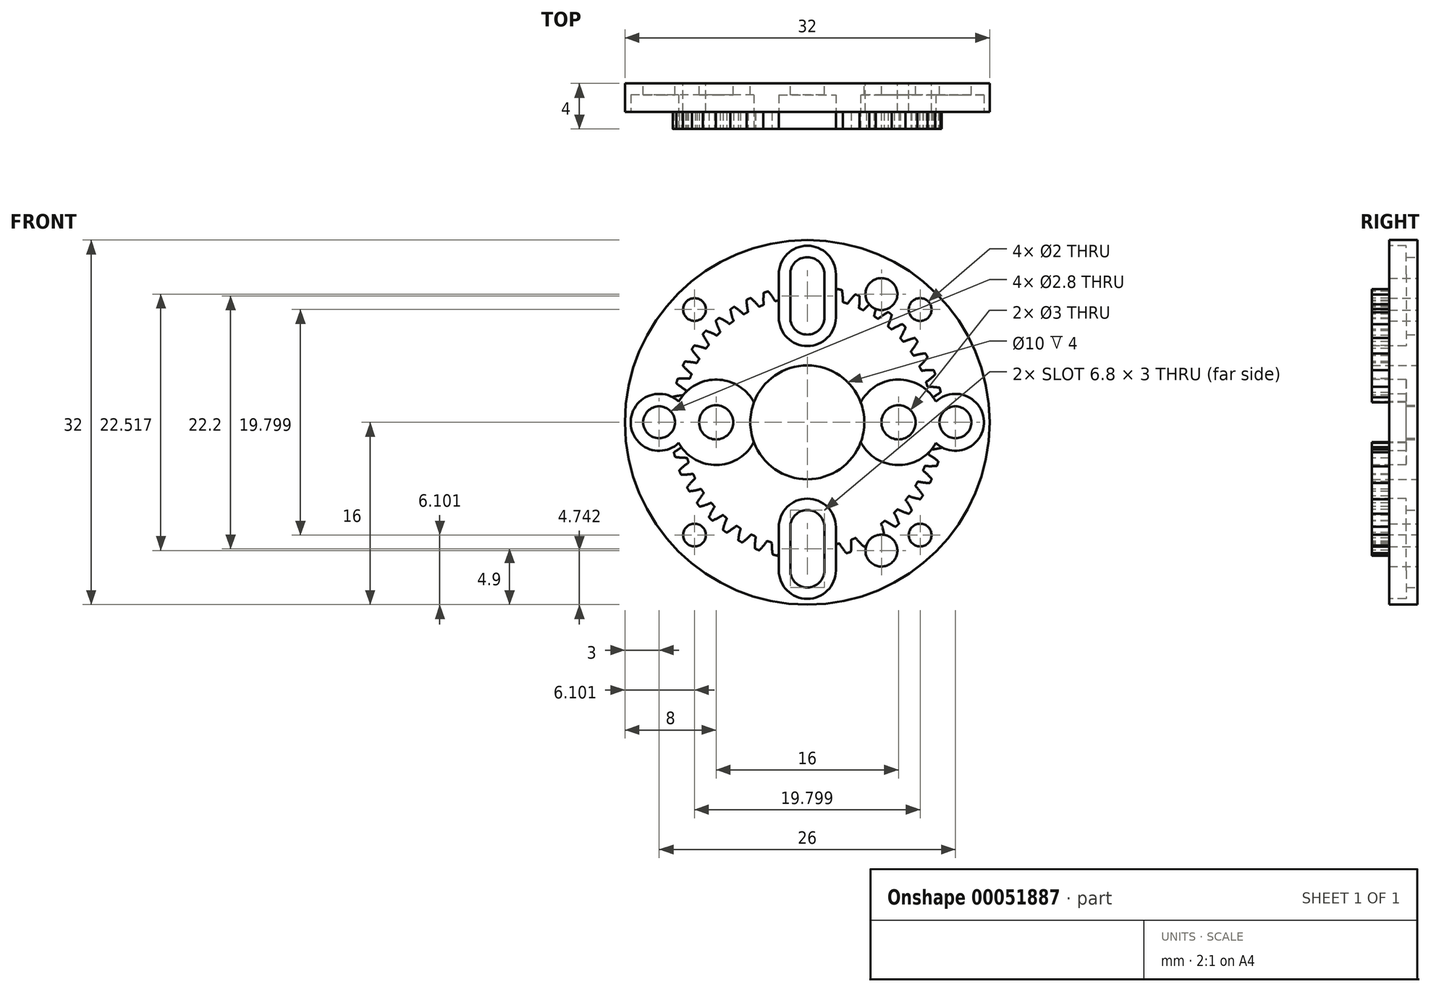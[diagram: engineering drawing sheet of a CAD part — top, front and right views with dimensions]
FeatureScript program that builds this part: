
annotation { "Feature Type Name" : "Feature", "Feature Type Description" : "" }
export const myFeature = defineFeature(function(context is Context, id is Id, definition is map)
    precondition{}
    {
        {
            var Q0;
            Q0=qCreatedBy(makeId("Front.planeOp"),FACE);
            var sketch = newSketch(context, id + "F0", { "sketchPlane" : qUnion([Q0])});
            skCircle(sketch, "E0", {"center": v(0, 0) * mm, "radius": 16 * mm});
            skSolve(sketch);
        }
        {
            var Q0;
            Q0=qCreatedBy(makeId("Front.planeOp"),FACE);
            var sketch = newSketch(context, id + "F1", { "sketchPlane" : qUnion([Q0])});
            skCircle(sketch, "E1", {"center": v(0, 0) * mm, "radius": 5 * mm});
            skLineSegment(sketch, "E2", {"start": v(0, 34) * mm, "end": v(0, -40.73) * mm, "construction": true});
            skLineSegment(sketch, "E3", {"start": v(35.1, 0) * mm, "end": v(-39.8, 0) * mm, "construction": true});
            skCircle(sketch, "E4", {"center": v(-13, 0) * mm, "radius": 1.4 * mm});
            skCircle(sketch, "E5", {"center": v(-8, 0) * mm, "radius": 1.5 * mm});
            skArc(sketch, "E6", {"start": v(1.5, 13) * mm, "mid": v(0, 14.5) * mm, "end": v(-1.5, 13) * mm});
            skArc(sketch, "E7", {"start": v(-1.5, 9.2) * mm, "mid": v(0, 7.7) * mm, "end": v(1.5, 9.2) * mm});
            skLineSegment(sketch, "E8", {"start": v(0, 0) * mm, "end": v(-31, 31) * mm, "construction": true});
            skCircle(sketch, "E9", {"center": v(-9.9, 9.9) * mm, "radius": 1 * mm});
            skLineSegment(sketch, "E10.left", {"start": v(-1.5, 13) * mm, "end": v(-1.5, 9.2) * mm});
            skLineSegment(sketch, "E10.right", {"start": v(1.5, 13) * mm, "end": v(1.5, 9.2) * mm});
            skArc(sketch, "E11.1.0", {"start": v(-1.5, -13) * mm, "mid": v(0, -14.5) * mm, "end": v(1.5, -13) * mm});
            skLineSegment(sketch, "E11.1.1", {"start": v(1.5, -13) * mm, "end": v(1.5, -9.2) * mm});
            skLineSegment(sketch, "E11.1.2", {"start": v(-1.5, -13) * mm, "end": v(-1.5, -9.2) * mm});
            skArc(sketch, "E11.1.3", {"start": v(1.5, -9.2) * mm, "mid": v(0, -7.7) * mm, "end": v(-1.5, -9.2) * mm});
            skCircle(sketch, "E11.1.4", {"center": v(13, 0) * mm, "radius": 1.4 * mm});
            skCircle(sketch, "E11.1.5", {"center": v(8, 0) * mm, "radius": 1.5 * mm});
            skCircle(sketch, "E12.1.0", {"center": v(6.5, -11.26) * mm, "radius": 1.4 * mm});
            skCircle(sketch, "E12.2.0", {"center": v(6.5, 11.26) * mm, "radius": 1.4 * mm});
            skCircle(sketch, "E13.1.0", {"center": v(-9.9, -9.9) * mm, "radius": 1 * mm});
            skCircle(sketch, "E13.2.0", {"center": v(9.9, -9.9) * mm, "radius": 1 * mm});
            skCircle(sketch, "E13.3.0", {"center": v(9.9, 9.9) * mm, "radius": 1 * mm});
            skSolve(sketch);
        }
        {
            var Q0;
            Q0 = qSketchRegion(id + "F0", true);
            extrude(context, id + "F2", {"entities" : qUnion([Q0]), "depth" : 4 * mm});
        }
        {
            var Q0;
            Q0 = qSketchRegion(id + "F1", true);
            extrude(context, id + "F3", {"entities" : qUnion([Q0]), "operationType" : NewBodyOperationType.REMOVE, "endBound" : BoundingType.THROUGH_ALL, "depth" : 25 * mm});
        }
        {
            var Q0;
            Q0=makeQuery(id+"F2.opExtrude","CAP_FACE",FACE,{"disambiguationData":[OSD([sQuery(id+"F0.wireOp",EDGE,"E0")])],"isStart":false});
            var sketch = newSketch(context, id + "F4", { "sketchPlane" : qUnion([Q0])});
            skArc(sketch, "E14", {"start": v(2.5, 13) * mm, "mid": v(0, 15.5) * mm, "end": v(-2.5, 13) * mm});
            skArc(sketch, "E15", {"start": v(-2.5, 9.2) * mm, "mid": v(0, 6.7) * mm, "end": v(2.5, 9.2) * mm});
            skArc(sketch, "E16", {"start": v(-11.28, 1.82) * mm, "mid": v(-15.5, 0) * mm, "end": v(-11.28, -1.82) * mm});
            skArc(sketch, "E17", {"start": v(-11.28, -1.82) * mm, "mid": v(-4.25, 0) * mm, "end": v(-11.28, 1.82) * mm});
            skLineSegment(sketch, "E18.left", {"start": v(-2.5, 13) * mm, "end": v(-2.5, 9.2) * mm});
            skLineSegment(sketch, "E18.right", {"start": v(2.5, 13) * mm, "end": v(2.5, 9.2) * mm});
            skArc(sketch, "E19.1.0", {"start": v(-2.5, -13) * mm, "mid": v(0, -15.5) * mm, "end": v(2.5, -13) * mm});
            skLineSegment(sketch, "E19.1.1", {"start": v(2.5, -13) * mm, "end": v(2.5, -9.2) * mm});
            skArc(sketch, "E19.1.2", {"start": v(2.5, -9.2) * mm, "mid": v(0, -6.7) * mm, "end": v(-2.5, -9.2) * mm});
            skLineSegment(sketch, "E19.1.3", {"start": v(-2.5, -13) * mm, "end": v(-2.5, -9.2) * mm});
            skArc(sketch, "E19.1.4", {"start": v(11.28, -1.82) * mm, "mid": v(15.5, 0) * mm, "end": v(11.28, 1.82) * mm});
            skArc(sketch, "E19.1.5", {"start": v(11.28, 1.82) * mm, "mid": v(4.25, 0) * mm, "end": v(11.28, -1.82) * mm});
            skPoint(sketch, "E19.center", {"position": v(0, 0) * mm});
            skSolve(sketch);
        }
        {
            var Q0;
            Q0 = qSketchRegion(id + "F4", true);
            extrude(context, id + "F5", {"entities" : qUnion([Q0]), "operationType" : NewBodyOperationType.REMOVE, "oppositeDirection" : true, "depth" : 3 * mm});
        }
        {
            var Q0;
            Q0=makeQuery(id+"F2.opExtrude","CAP_FACE",FACE,{"disambiguationData":[OSD([sQuery(id+"F0.wireOp",EDGE,"E0")])],"isStart":false});
            var sketch = newSketch(context, id + "F6", { "sketchPlane" : qUnion([Q0])});
            skCircle(sketch, "E20", {"center": v(0, 0) * mm, "radius": 16 * mm});
            skCircle(sketch, "E21", {"center": v(0, 0) * mm, "radius": 12 * mm, "construction": true});
            skCircle(sketch, "E22", {"center": v(0, 0) * mm, "radius": 11.5 * mm, "construction": true});
            skCircle(sketch, "E23", {"center": v(0, 0) * mm, "radius": 11 * mm, "construction": true});
            skLineSegment(sketch, "E24", {"start": v(0, 0) * mm, "end": v(0, 20.22) * mm, "construction": true});
            skLineSegment(sketch, "E25", {"start": v(0, 0) * mm, "end": v(-0.7, 20.22) * mm, "construction": true});
            skLineSegment(sketch, "E26", {"start": v(0, 11.5) * mm, "end": v(-8.2, 11.5) * mm, "construction": true});
            skLineSegment(sketch, "E27", {"start": v(0, 11.5) * mm, "end": v(-7.4, 8.8) * mm, "construction": true});
            skCircle(sketch, "E28", {"center": v(0, 11.5) * mm, "radius": 5.75 * mm, "construction": true});
            skCircle(sketch, "E29", {"center": v(-5.4, 9.53) * mm, "radius": 5.75 * mm, "construction": true});
            skArc(sketch, "E30", {"start": v(-0.2, 12) * mm, "mid": v(0, 11.5) * mm, "end": v(0.16, 11) * mm, "construction": true});
            skArc(sketch, "E31.MirrorCS", {"start": v(-0.61, 11.98) * mm, "mid": v(-0.78, 11.48) * mm, "end": v(-0.9, 10.96) * mm, "construction": true});
            skArc(sketch, "E32", {"start": v(-0.62, 11.95) * mm, "mid": v(-0.78, 11.48) * mm, "end": v(-0.9, 11) * mm});
            skArc(sketch, "E33", {"start": v(-0.58, 11.99) * mm, "mid": v(-0.4, 12) * mm, "end": v(-0.24, 12) * mm});
            skArc(sketch, "E34", {"start": v(-0.2, 11.97) * mm, "mid": v(0, 11.5) * mm, "end": v(0.15, 11.04) * mm});
            skArc(sketch, "E35", {"start": v(-0.94, 10.96) * mm, "mid": v(0.38, -11) * mm, "end": v(0.2, 11) * mm});
            skPoint(sketch, "E36.visualSharp", {"position": v(-0.9, 10.96) * mm});
            skArc(sketch, "E36.filletArc", {"start": v(-0.94, 10.96) * mm, "mid": v(-0.92, 10.97) * mm, "end": v(-0.9, 11) * mm});
            skPoint(sketch, "E37.visualSharp", {"position": v(-0.61, 11.98) * mm});
            skArc(sketch, "E37.filletArc", {"start": v(-0.58, 11.99) * mm, "mid": v(-0.6, 11.98) * mm, "end": v(-0.62, 11.95) * mm});
            skPoint(sketch, "E38.visualSharp", {"position": v(-0.2, 12) * mm});
            skArc(sketch, "E38.filletArc", {"start": v(-0.2, 11.97) * mm, "mid": v(-0.21, 12) * mm, "end": v(-0.24, 12) * mm});
            skPoint(sketch, "E39.visualSharp", {"position": v(0.16, 11) * mm});
            skArc(sketch, "E39.filletArc", {"start": v(0.15, 11.04) * mm, "mid": v(0.16, 11) * mm, "end": v(0.2, 11) * mm});
            skArc(sketch, "E40.1.0", {"start": v(-2.43, 10.73) * mm, "mid": v(-2.4, 10.75) * mm, "end": v(-2.39, 10.77) * mm});
            skArc(sketch, "E40.1.1", {"start": v(-2.24, 11.76) * mm, "mid": v(-2.34, 11.27) * mm, "end": v(-2.39, 10.77) * mm});
            skArc(sketch, "E40.1.2", {"start": v(-2.2, 11.8) * mm, "mid": v(-2.23, 11.78) * mm, "end": v(-2.24, 11.76) * mm});
            skArc(sketch, "E40.1.3", {"start": v(-2.2, 11.8) * mm, "mid": v(-2.04, 11.83) * mm, "end": v(-1.87, 11.85) * mm});
            skArc(sketch, "E40.1.4", {"start": v(-1.82, 11.83) * mm, "mid": v(-1.84, 11.85) * mm, "end": v(-1.87, 11.85) * mm});
            skArc(sketch, "E40.1.5", {"start": v(-1.82, 11.83) * mm, "mid": v(-1.57, 11.4) * mm, "end": v(-1.36, 10.95) * mm});
            skArc(sketch, "E40.1.6", {"start": v(-1.36, 10.95) * mm, "mid": v(-1.34, 10.93) * mm, "end": v(-1.3, 10.92) * mm});
            skArc(sketch, "E40.2.0", {"start": v(-3.87, 10.3) * mm, "mid": v(-3.84, 10.32) * mm, "end": v(-3.83, 10.35) * mm});
            skArc(sketch, "E40.2.1", {"start": v(-3.82, 11.34) * mm, "mid": v(-3.85, 10.85) * mm, "end": v(-3.83, 10.35) * mm});
            skArc(sketch, "E40.2.2", {"start": v(-3.8, 11.39) * mm, "mid": v(-3.81, 11.37) * mm, "end": v(-3.82, 11.34) * mm});
            skArc(sketch, "E40.2.3", {"start": v(-3.8, 11.39) * mm, "mid": v(-3.63, 11.44) * mm, "end": v(-3.47, 11.49) * mm});
            skArc(sketch, "E40.2.4", {"start": v(-3.42, 11.47) * mm, "mid": v(-3.44, 11.49) * mm, "end": v(-3.47, 11.49) * mm});
            skArc(sketch, "E40.2.5", {"start": v(-3.42, 11.47) * mm, "mid": v(-3.1, 11.08) * mm, "end": v(-2.84, 10.67) * mm});
            skArc(sketch, "E40.2.6", {"start": v(-2.84, 10.67) * mm, "mid": v(-2.81, 10.65) * mm, "end": v(-2.78, 10.64) * mm});
            skArc(sketch, "E40.3.0", {"start": v(-5.23, 9.68) * mm, "mid": v(-5.21, 9.7) * mm, "end": v(-5.2, 9.73) * mm});
            skArc(sketch, "E40.3.1", {"start": v(-5.33, 10.72) * mm, "mid": v(-5.3, 10.22) * mm, "end": v(-5.2, 9.73) * mm});
            skArc(sketch, "E40.3.2", {"start": v(-5.3, 10.76) * mm, "mid": v(-5.33, 10.74) * mm, "end": v(-5.33, 10.72) * mm});
            skArc(sketch, "E40.3.3", {"start": v(-5.3, 10.76) * mm, "mid": v(-5.15, 10.84) * mm, "end": v(-5, 10.9) * mm});
            skArc(sketch, "E40.3.4", {"start": v(-4.95, 10.9) * mm, "mid": v(-4.97, 10.91) * mm, "end": v(-5, 10.9) * mm});
            skArc(sketch, "E40.3.5", {"start": v(-4.95, 10.9) * mm, "mid": v(-4.59, 10.56) * mm, "end": v(-4.26, 10.18) * mm});
            skArc(sketch, "E40.3.6", {"start": v(-4.26, 10.18) * mm, "mid": v(-4.23, 10.16) * mm, "end": v(-4.2, 10.17) * mm});
            skArc(sketch, "E40.4.0", {"start": v(-6.5, 8.87) * mm, "mid": v(-6.48, 8.9) * mm, "end": v(-6.48, 8.93) * mm});
            skArc(sketch, "E40.4.1", {"start": v(-6.74, 9.9) * mm, "mid": v(-6.63, 9.4) * mm, "end": v(-6.48, 8.93) * mm});
            skArc(sketch, "E40.4.2", {"start": v(-6.72, 9.94) * mm, "mid": v(-6.74, 9.92) * mm, "end": v(-6.74, 9.9) * mm});
            skArc(sketch, "E40.4.3", {"start": v(-6.72, 9.94) * mm, "mid": v(-6.58, 10.03) * mm, "end": v(-6.44, 10.13) * mm});
            skArc(sketch, "E40.4.4", {"start": v(-6.38, 10.13) * mm, "mid": v(-6.41, 10.13) * mm, "end": v(-6.44, 10.13) * mm});
            skArc(sketch, "E40.4.5", {"start": v(-6.38, 10.13) * mm, "mid": v(-5.98, 9.83) * mm, "end": v(-5.6, 9.5) * mm});
            skArc(sketch, "E40.4.6", {"start": v(-5.6, 9.5) * mm, "mid": v(-5.58, 9.5) * mm, "end": v(-5.55, 9.5) * mm});
            skArc(sketch, "E40.5.0", {"start": v(-7.65, 7.9) * mm, "mid": v(-7.63, 7.93) * mm, "end": v(-7.64, 7.96) * mm});
            skArc(sketch, "E40.5.1", {"start": v(-8.03, 8.88) * mm, "mid": v(-7.85, 8.41) * mm, "end": v(-7.64, 7.96) * mm});
            skArc(sketch, "E40.5.2", {"start": v(-8.01, 8.93) * mm, "mid": v(-8.03, 8.9) * mm, "end": v(-8.03, 8.88) * mm});
            skArc(sketch, "E40.5.3", {"start": v(-8.01, 8.93) * mm, "mid": v(-7.89, 9.04) * mm, "end": v(-7.76, 9.15) * mm});
            skArc(sketch, "E40.5.4", {"start": v(-7.7, 9.16) * mm, "mid": v(-7.73, 9.17) * mm, "end": v(-7.76, 9.15) * mm});
            skArc(sketch, "E40.5.5", {"start": v(-7.7, 9.16) * mm, "mid": v(-7.27, 8.93) * mm, "end": v(-6.85, 8.65) * mm});
            skArc(sketch, "E40.5.6", {"start": v(-6.85, 8.65) * mm, "mid": v(-6.82, 8.64) * mm, "end": v(-6.79, 8.65) * mm});
            skArc(sketch, "E40.6.0", {"start": v(-8.65, 6.79) * mm, "mid": v(-8.64, 6.82) * mm, "end": v(-8.65, 6.85) * mm});
            skArc(sketch, "E40.6.1", {"start": v(-9.16, 7.7) * mm, "mid": v(-8.93, 7.27) * mm, "end": v(-8.65, 6.85) * mm});
            skArc(sketch, "E40.6.2", {"start": v(-9.15, 7.76) * mm, "mid": v(-9.17, 7.73) * mm, "end": v(-9.16, 7.7) * mm});
            skArc(sketch, "E40.6.3", {"start": v(-9.15, 7.76) * mm, "mid": v(-9.04, 7.89) * mm, "end": v(-8.93, 8.01) * mm});
            skArc(sketch, "E40.6.4", {"start": v(-8.88, 8.03) * mm, "mid": v(-8.9, 8.03) * mm, "end": v(-8.93, 8.01) * mm});
            skArc(sketch, "E40.6.5", {"start": v(-8.88, 8.03) * mm, "mid": v(-8.41, 7.85) * mm, "end": v(-7.96, 7.64) * mm});
            skArc(sketch, "E40.6.6", {"start": v(-7.96, 7.64) * mm, "mid": v(-7.93, 7.63) * mm, "end": v(-7.9, 7.65) * mm});
            skArc(sketch, "E40.7.0", {"start": v(-9.5, 5.55) * mm, "mid": v(-9.5, 5.58) * mm, "end": v(-9.5, 5.6) * mm});
            skArc(sketch, "E40.7.1", {"start": v(-10.13, 6.38) * mm, "mid": v(-9.83, 5.98) * mm, "end": v(-9.5, 5.6) * mm});
            skArc(sketch, "E40.7.2", {"start": v(-10.13, 6.44) * mm, "mid": v(-10.13, 6.41) * mm, "end": v(-10.13, 6.38) * mm});
            skArc(sketch, "E40.7.3", {"start": v(-10.13, 6.44) * mm, "mid": v(-10.03, 6.58) * mm, "end": v(-9.94, 6.72) * mm});
            skArc(sketch, "E40.7.4", {"start": v(-9.9, 6.74) * mm, "mid": v(-9.92, 6.74) * mm, "end": v(-9.94, 6.72) * mm});
            skArc(sketch, "E40.7.5", {"start": v(-9.9, 6.74) * mm, "mid": v(-9.4, 6.63) * mm, "end": v(-8.93, 6.48) * mm});
            skArc(sketch, "E40.7.6", {"start": v(-8.93, 6.48) * mm, "mid": v(-8.9, 6.48) * mm, "end": v(-8.87, 6.5) * mm});
            skArc(sketch, "E40.8.0", {"start": v(-10.17, 4.2) * mm, "mid": v(-10.16, 4.23) * mm, "end": v(-10.18, 4.26) * mm});
            skArc(sketch, "E40.8.1", {"start": v(-10.9, 4.95) * mm, "mid": v(-10.56, 4.59) * mm, "end": v(-10.18, 4.26) * mm});
            skArc(sketch, "E40.8.2", {"start": v(-10.9, 5) * mm, "mid": v(-10.91, 4.97) * mm, "end": v(-10.9, 4.95) * mm});
            skArc(sketch, "E40.8.3", {"start": v(-10.9, 5) * mm, "mid": v(-10.84, 5.15) * mm, "end": v(-10.76, 5.3) * mm});
            skArc(sketch, "E40.8.4", {"start": v(-10.72, 5.33) * mm, "mid": v(-10.74, 5.33) * mm, "end": v(-10.76, 5.3) * mm});
            skArc(sketch, "E40.8.5", {"start": v(-10.72, 5.33) * mm, "mid": v(-10.22, 5.3) * mm, "end": v(-9.73, 5.2) * mm});
            skArc(sketch, "E40.8.6", {"start": v(-9.73, 5.2) * mm, "mid": v(-9.7, 5.21) * mm, "end": v(-9.68, 5.23) * mm});
            skArc(sketch, "E40.9.0", {"start": v(-10.64, 2.78) * mm, "mid": v(-10.65, 2.81) * mm, "end": v(-10.67, 2.84) * mm});
            skArc(sketch, "E40.9.1", {"start": v(-11.47, 3.42) * mm, "mid": v(-11.08, 3.1) * mm, "end": v(-10.67, 2.84) * mm});
            skArc(sketch, "E40.9.2", {"start": v(-11.49, 3.47) * mm, "mid": v(-11.49, 3.44) * mm, "end": v(-11.47, 3.42) * mm});
            skArc(sketch, "E40.9.3", {"start": v(-11.49, 3.47) * mm, "mid": v(-11.44, 3.63) * mm, "end": v(-11.39, 3.8) * mm});
            skArc(sketch, "E40.9.4", {"start": v(-11.34, 3.82) * mm, "mid": v(-11.37, 3.81) * mm, "end": v(-11.39, 3.8) * mm});
            skArc(sketch, "E40.9.5", {"start": v(-11.34, 3.82) * mm, "mid": v(-10.85, 3.85) * mm, "end": v(-10.35, 3.83) * mm});
            skArc(sketch, "E40.9.6", {"start": v(-10.35, 3.83) * mm, "mid": v(-10.32, 3.84) * mm, "end": v(-10.3, 3.87) * mm});
            skArc(sketch, "E40.10.0", {"start": v(-10.92, 1.3) * mm, "mid": v(-10.93, 1.34) * mm, "end": v(-10.95, 1.36) * mm});
            skArc(sketch, "E40.10.1", {"start": v(-11.83, 1.82) * mm, "mid": v(-11.4, 1.57) * mm, "end": v(-10.95, 1.36) * mm});
            skArc(sketch, "E40.10.2", {"start": v(-11.85, 1.87) * mm, "mid": v(-11.85, 1.84) * mm, "end": v(-11.83, 1.82) * mm});
            skArc(sketch, "E40.10.3", {"start": v(-11.85, 1.87) * mm, "mid": v(-11.83, 2.04) * mm, "end": v(-11.8, 2.2) * mm});
            skArc(sketch, "E40.10.4", {"start": v(-11.76, 2.24) * mm, "mid": v(-11.78, 2.23) * mm, "end": v(-11.8, 2.2) * mm});
            skArc(sketch, "E40.10.5", {"start": v(-11.76, 2.24) * mm, "mid": v(-11.27, 2.34) * mm, "end": v(-10.77, 2.39) * mm});
            skArc(sketch, "E40.10.6", {"start": v(-10.77, 2.39) * mm, "mid": v(-10.75, 2.4) * mm, "end": v(-10.73, 2.43) * mm});
            skArc(sketch, "E40.11.0", {"start": v(-11, -0.2) * mm, "mid": v(-11, -0.16) * mm, "end": v(-11.04, -0.15) * mm});
            skArc(sketch, "E40.11.1", {"start": v(-11.97, 0.2) * mm, "mid": v(-11.5, 0) * mm, "end": v(-11.04, -0.15) * mm});
            skArc(sketch, "E40.11.2", {"start": v(-12, 0.24) * mm, "mid": v(-12, 0.21) * mm, "end": v(-11.97, 0.2) * mm});
            skArc(sketch, "E40.11.3", {"start": v(-12, 0.24) * mm, "mid": v(-12, 0.4) * mm, "end": v(-11.99, 0.58) * mm});
            skArc(sketch, "E40.11.4", {"start": v(-11.95, 0.62) * mm, "mid": v(-11.98, 0.6) * mm, "end": v(-11.99, 0.58) * mm});
            skArc(sketch, "E40.11.5", {"start": v(-11.95, 0.62) * mm, "mid": v(-11.48, 0.78) * mm, "end": v(-11, 0.9) * mm});
            skArc(sketch, "E40.11.6", {"start": v(-11, 0.9) * mm, "mid": v(-10.97, 0.92) * mm, "end": v(-10.96, 0.94) * mm});
            skArc(sketch, "E40.12.0", {"start": v(-10.87, -1.7) * mm, "mid": v(-10.88, -1.66) * mm, "end": v(-10.91, -1.65) * mm});
            skArc(sketch, "E40.12.1", {"start": v(-11.88, -1.44) * mm, "mid": v(-11.4, -1.56) * mm, "end": v(-10.91, -1.65) * mm});
            skArc(sketch, "E40.12.2", {"start": v(-11.92, -1.4) * mm, "mid": v(-11.9, -1.42) * mm, "end": v(-11.88, -1.44) * mm});
            skArc(sketch, "E40.12.3", {"start": v(-11.92, -1.4) * mm, "mid": v(-11.94, -1.23) * mm, "end": v(-11.95, -1.06) * mm});
            skArc(sketch, "E40.12.4", {"start": v(-11.93, -1.01) * mm, "mid": v(-11.95, -1.03) * mm, "end": v(-11.95, -1.06) * mm});
            skArc(sketch, "E40.12.5", {"start": v(-11.93, -1.01) * mm, "mid": v(-11.48, -0.79) * mm, "end": v(-11.02, -0.6) * mm});
            skArc(sketch, "E40.12.6", {"start": v(-11.02, -0.6) * mm, "mid": v(-11, -0.59) * mm, "end": v(-10.99, -0.56) * mm});
            skArc(sketch, "E40.13.0", {"start": v(-10.54, -3.15) * mm, "mid": v(-10.56, -3.13) * mm, "end": v(-10.59, -3.12) * mm});
            skArc(sketch, "E40.13.1", {"start": v(-11.58, -3.04) * mm, "mid": v(-11.08, -3.1) * mm, "end": v(-10.59, -3.12) * mm});
            skArc(sketch, "E40.13.2", {"start": v(-11.62, -3) * mm, "mid": v(-11.6, -3.03) * mm, "end": v(-11.58, -3.04) * mm});
            skArc(sketch, "E40.13.3", {"start": v(-11.62, -3) * mm, "mid": v(-11.66, -2.84) * mm, "end": v(-11.7, -2.68) * mm});
            skArc(sketch, "E40.13.4", {"start": v(-11.68, -2.63) * mm, "mid": v(-11.7, -2.65) * mm, "end": v(-11.7, -2.68) * mm});
            skArc(sketch, "E40.13.5", {"start": v(-11.68, -2.63) * mm, "mid": v(-11.27, -2.35) * mm, "end": v(-10.83, -2.1) * mm});
            skArc(sketch, "E40.13.6", {"start": v(-10.83, -2.1) * mm, "mid": v(-10.81, -2.08) * mm, "end": v(-10.8, -2.05) * mm});
            skArc(sketch, "E40.14.0", {"start": v(-10.01, -4.56) * mm, "mid": v(-10.03, -4.54) * mm, "end": v(-10.06, -4.53) * mm});
            skArc(sketch, "E40.14.1", {"start": v(-11.06, -4.6) * mm, "mid": v(-10.56, -4.58) * mm, "end": v(-10.06, -4.53) * mm});
            skArc(sketch, "E40.14.2", {"start": v(-11.1, -4.56) * mm, "mid": v(-11.08, -4.58) * mm, "end": v(-11.06, -4.6) * mm});
            skArc(sketch, "E40.14.3", {"start": v(-11.1, -4.56) * mm, "mid": v(-11.16, -4.4) * mm, "end": v(-11.22, -4.24) * mm});
            skArc(sketch, "E40.14.4", {"start": v(-11.21, -4.2) * mm, "mid": v(-11.23, -4.22) * mm, "end": v(-11.22, -4.24) * mm});
            skArc(sketch, "E40.14.5", {"start": v(-11.21, -4.2) * mm, "mid": v(-10.84, -3.86) * mm, "end": v(-10.45, -3.56) * mm});
            skArc(sketch, "E40.14.6", {"start": v(-10.45, -3.56) * mm, "mid": v(-10.43, -3.53) * mm, "end": v(-10.43, -3.5) * mm});
            skArc(sketch, "E40.15.0", {"start": v(-9.3, -5.88) * mm, "mid": v(-9.32, -5.86) * mm, "end": v(-9.35, -5.86) * mm});
            skArc(sketch, "E40.15.1", {"start": v(-10.33, -6.05) * mm, "mid": v(-9.84, -5.98) * mm, "end": v(-9.35, -5.86) * mm});
            skArc(sketch, "E40.15.2", {"start": v(-10.38, -6.03) * mm, "mid": v(-10.36, -6.05) * mm, "end": v(-10.33, -6.05) * mm});
            skArc(sketch, "E40.15.3", {"start": v(-10.38, -6.03) * mm, "mid": v(-10.46, -5.88) * mm, "end": v(-10.54, -5.73) * mm});
            skArc(sketch, "E40.15.4", {"start": v(-10.54, -5.68) * mm, "mid": v(-10.55, -5.7) * mm, "end": v(-10.54, -5.73) * mm});
            skArc(sketch, "E40.15.5", {"start": v(-10.54, -5.68) * mm, "mid": v(-10.22, -5.3) * mm, "end": v(-9.87, -4.95) * mm});
            skArc(sketch, "E40.15.6", {"start": v(-9.87, -4.95) * mm, "mid": v(-9.85, -4.92) * mm, "end": v(-9.85, -4.89) * mm});
            skArc(sketch, "E40.16.0", {"start": v(-8.4, -7.1) * mm, "mid": v(-8.44, -7.08) * mm, "end": v(-8.47, -7.08) * mm});
            skArc(sketch, "E40.16.1", {"start": v(-9.4, -7.4) * mm, "mid": v(-8.93, -7.26) * mm, "end": v(-8.47, -7.08) * mm});
            skArc(sketch, "E40.16.2", {"start": v(-9.46, -7.38) * mm, "mid": v(-9.44, -7.4) * mm, "end": v(-9.4, -7.4) * mm});
            skArc(sketch, "E40.16.3", {"start": v(-9.46, -7.38) * mm, "mid": v(-9.56, -7.25) * mm, "end": v(-9.66, -7.12) * mm});
            skArc(sketch, "E40.16.4", {"start": v(-9.67, -7.06) * mm, "mid": v(-9.67, -7.09) * mm, "end": v(-9.66, -7.12) * mm});
            skArc(sketch, "E40.16.5", {"start": v(-9.67, -7.06) * mm, "mid": v(-9.4, -6.64) * mm, "end": v(-9.1, -6.24) * mm});
            skArc(sketch, "E40.16.6", {"start": v(-9.1, -6.24) * mm, "mid": v(-9.09, -6.21) * mm, "end": v(-9.1, -6.18) * mm});
            skArc(sketch, "E40.17.0", {"start": v(-7.36, -8.17) * mm, "mid": v(-7.4, -8.16) * mm, "end": v(-7.42, -8.17) * mm});
            skArc(sketch, "E40.17.1", {"start": v(-8.31, -8.61) * mm, "mid": v(-7.86, -8.4) * mm, "end": v(-7.42, -8.17) * mm});
            skArc(sketch, "E40.17.2", {"start": v(-8.36, -8.6) * mm, "mid": v(-8.34, -8.62) * mm, "end": v(-8.31, -8.61) * mm});
            skArc(sketch, "E40.17.3", {"start": v(-8.36, -8.6) * mm, "mid": v(-8.49, -8.49) * mm, "end": v(-8.6, -8.36) * mm});
            skArc(sketch, "E40.17.4", {"start": v(-8.61, -8.31) * mm, "mid": v(-8.62, -8.34) * mm, "end": v(-8.6, -8.36) * mm});
            skArc(sketch, "E40.17.5", {"start": v(-8.61, -8.31) * mm, "mid": v(-8.4, -7.86) * mm, "end": v(-8.17, -7.42) * mm});
            skArc(sketch, "E40.17.6", {"start": v(-8.17, -7.42) * mm, "mid": v(-8.16, -7.4) * mm, "end": v(-8.17, -7.36) * mm});
            skArc(sketch, "E40.18.0", {"start": v(-6.18, -9.1) * mm, "mid": v(-6.21, -9.09) * mm, "end": v(-6.24, -9.1) * mm});
            skArc(sketch, "E40.18.1", {"start": v(-7.06, -9.67) * mm, "mid": v(-6.64, -9.4) * mm, "end": v(-6.24, -9.1) * mm});
            skArc(sketch, "E40.18.2", {"start": v(-7.12, -9.66) * mm, "mid": v(-7.09, -9.67) * mm, "end": v(-7.06, -9.67) * mm});
            skArc(sketch, "E40.18.3", {"start": v(-7.12, -9.66) * mm, "mid": v(-7.25, -9.56) * mm, "end": v(-7.38, -9.46) * mm});
            skArc(sketch, "E40.18.4", {"start": v(-7.4, -9.4) * mm, "mid": v(-7.4, -9.44) * mm, "end": v(-7.38, -9.46) * mm});
            skArc(sketch, "E40.18.5", {"start": v(-7.4, -9.4) * mm, "mid": v(-7.26, -8.93) * mm, "end": v(-7.08, -8.47) * mm});
            skArc(sketch, "E40.18.6", {"start": v(-7.08, -8.47) * mm, "mid": v(-7.08, -8.44) * mm, "end": v(-7.1, -8.4) * mm});
            skArc(sketch, "E40.19.0", {"start": v(-4.89, -9.85) * mm, "mid": v(-4.92, -9.85) * mm, "end": v(-4.95, -9.87) * mm});
            skArc(sketch, "E40.19.1", {"start": v(-5.68, -10.54) * mm, "mid": v(-5.3, -10.22) * mm, "end": v(-4.95, -9.87) * mm});
            skArc(sketch, "E40.19.2", {"start": v(-5.73, -10.54) * mm, "mid": v(-5.7, -10.55) * mm, "end": v(-5.68, -10.54) * mm});
            skArc(sketch, "E40.19.3", {"start": v(-5.73, -10.54) * mm, "mid": v(-5.88, -10.46) * mm, "end": v(-6.03, -10.38) * mm});
            skArc(sketch, "E40.19.4", {"start": v(-6.05, -10.33) * mm, "mid": v(-6.05, -10.36) * mm, "end": v(-6.03, -10.38) * mm});
            skArc(sketch, "E40.19.5", {"start": v(-6.05, -10.33) * mm, "mid": v(-5.98, -9.84) * mm, "end": v(-5.86, -9.35) * mm});
            skArc(sketch, "E40.19.6", {"start": v(-5.86, -9.35) * mm, "mid": v(-5.86, -9.32) * mm, "end": v(-5.88, -9.3) * mm});
            skArc(sketch, "E40.20.0", {"start": v(-3.5, -10.43) * mm, "mid": v(-3.53, -10.43) * mm, "end": v(-3.56, -10.45) * mm});
            skArc(sketch, "E40.20.1", {"start": v(-4.2, -11.21) * mm, "mid": v(-3.86, -10.84) * mm, "end": v(-3.56, -10.45) * mm});
            skArc(sketch, "E40.20.2", {"start": v(-4.24, -11.22) * mm, "mid": v(-4.22, -11.23) * mm, "end": v(-4.2, -11.21) * mm});
            skArc(sketch, "E40.20.3", {"start": v(-4.24, -11.22) * mm, "mid": v(-4.4, -11.16) * mm, "end": v(-4.56, -11.1) * mm});
            skArc(sketch, "E40.20.4", {"start": v(-4.6, -11.06) * mm, "mid": v(-4.58, -11.08) * mm, "end": v(-4.56, -11.1) * mm});
            skArc(sketch, "E40.20.5", {"start": v(-4.6, -11.06) * mm, "mid": v(-4.58, -10.56) * mm, "end": v(-4.53, -10.06) * mm});
            skArc(sketch, "E40.20.6", {"start": v(-4.53, -10.06) * mm, "mid": v(-4.54, -10.03) * mm, "end": v(-4.56, -10.01) * mm});
            skArc(sketch, "E40.21.0", {"start": v(-2.05, -10.8) * mm, "mid": v(-2.08, -10.81) * mm, "end": v(-2.1, -10.83) * mm});
            skArc(sketch, "E40.21.1", {"start": v(-2.63, -11.68) * mm, "mid": v(-2.35, -11.27) * mm, "end": v(-2.1, -10.83) * mm});
            skArc(sketch, "E40.21.2", {"start": v(-2.68, -11.7) * mm, "mid": v(-2.65, -11.7) * mm, "end": v(-2.63, -11.68) * mm});
            skArc(sketch, "E40.21.3", {"start": v(-2.68, -11.7) * mm, "mid": v(-2.84, -11.66) * mm, "end": v(-3, -11.62) * mm});
            skArc(sketch, "E40.21.4", {"start": v(-3.04, -11.58) * mm, "mid": v(-3.03, -11.6) * mm, "end": v(-3, -11.62) * mm});
            skArc(sketch, "E40.21.5", {"start": v(-3.04, -11.58) * mm, "mid": v(-3.1, -11.08) * mm, "end": v(-3.12, -10.59) * mm});
            skArc(sketch, "E40.21.6", {"start": v(-3.12, -10.59) * mm, "mid": v(-3.13, -10.56) * mm, "end": v(-3.15, -10.54) * mm});
            skArc(sketch, "E40.22.0", {"start": v(-0.56, -10.99) * mm, "mid": v(-0.59, -11) * mm, "end": v(-0.6, -11.02) * mm});
            skArc(sketch, "E40.22.1", {"start": v(-1.01, -11.93) * mm, "mid": v(-0.79, -11.48) * mm, "end": v(-0.6, -11.02) * mm});
            skArc(sketch, "E40.22.2", {"start": v(-1.06, -11.95) * mm, "mid": v(-1.03, -11.95) * mm, "end": v(-1.01, -11.93) * mm});
            skArc(sketch, "E40.22.3", {"start": v(-1.06, -11.95) * mm, "mid": v(-1.23, -11.94) * mm, "end": v(-1.4, -11.92) * mm});
            skArc(sketch, "E40.22.4", {"start": v(-1.44, -11.88) * mm, "mid": v(-1.42, -11.9) * mm, "end": v(-1.4, -11.92) * mm});
            skArc(sketch, "E40.22.5", {"start": v(-1.44, -11.88) * mm, "mid": v(-1.56, -11.4) * mm, "end": v(-1.65, -10.91) * mm});
            skArc(sketch, "E40.22.6", {"start": v(-1.65, -10.91) * mm, "mid": v(-1.66, -10.88) * mm, "end": v(-1.7, -10.87) * mm});
            skArc(sketch, "E40.23.0", {"start": v(0.94, -10.96) * mm, "mid": v(0.92, -10.97) * mm, "end": v(0.9, -11) * mm});
            skArc(sketch, "E40.23.1", {"start": v(0.62, -11.95) * mm, "mid": v(0.78, -11.48) * mm, "end": v(0.9, -11) * mm});
            skArc(sketch, "E40.23.2", {"start": v(0.58, -11.99) * mm, "mid": v(0.6, -11.98) * mm, "end": v(0.62, -11.95) * mm});
            skArc(sketch, "E40.23.3", {"start": v(0.58, -11.99) * mm, "mid": v(0.4, -12) * mm, "end": v(0.24, -12) * mm});
            skArc(sketch, "E40.23.4", {"start": v(0.2, -11.97) * mm, "mid": v(0.21, -12) * mm, "end": v(0.24, -12) * mm});
            skArc(sketch, "E40.23.5", {"start": v(0.2, -11.97) * mm, "mid": v(0, -11.5) * mm, "end": v(-0.15, -11.04) * mm});
            skArc(sketch, "E40.23.6", {"start": v(-0.15, -11.04) * mm, "mid": v(-0.16, -11) * mm, "end": v(-0.2, -11) * mm});
            skArc(sketch, "E40.24.0", {"start": v(2.43, -10.73) * mm, "mid": v(2.4, -10.75) * mm, "end": v(2.39, -10.77) * mm});
            skArc(sketch, "E40.24.1", {"start": v(2.24, -11.76) * mm, "mid": v(2.34, -11.27) * mm, "end": v(2.39, -10.77) * mm});
            skArc(sketch, "E40.24.2", {"start": v(2.2, -11.8) * mm, "mid": v(2.23, -11.78) * mm, "end": v(2.24, -11.76) * mm});
            skArc(sketch, "E40.24.3", {"start": v(2.2, -11.8) * mm, "mid": v(2.04, -11.83) * mm, "end": v(1.87, -11.85) * mm});
            skArc(sketch, "E40.24.4", {"start": v(1.82, -11.83) * mm, "mid": v(1.84, -11.85) * mm, "end": v(1.87, -11.85) * mm});
            skArc(sketch, "E40.24.5", {"start": v(1.82, -11.83) * mm, "mid": v(1.57, -11.4) * mm, "end": v(1.36, -10.95) * mm});
            skArc(sketch, "E40.24.6", {"start": v(1.36, -10.95) * mm, "mid": v(1.34, -10.93) * mm, "end": v(1.3, -10.92) * mm});
            skArc(sketch, "E40.25.0", {"start": v(3.87, -10.3) * mm, "mid": v(3.84, -10.32) * mm, "end": v(3.83, -10.35) * mm});
            skArc(sketch, "E40.25.1", {"start": v(3.82, -11.34) * mm, "mid": v(3.85, -10.85) * mm, "end": v(3.83, -10.35) * mm});
            skArc(sketch, "E40.25.2", {"start": v(3.8, -11.39) * mm, "mid": v(3.81, -11.37) * mm, "end": v(3.82, -11.34) * mm});
            skArc(sketch, "E40.25.3", {"start": v(3.8, -11.39) * mm, "mid": v(3.63, -11.44) * mm, "end": v(3.47, -11.49) * mm});
            skArc(sketch, "E40.25.4", {"start": v(3.42, -11.47) * mm, "mid": v(3.44, -11.49) * mm, "end": v(3.47, -11.49) * mm});
            skArc(sketch, "E40.25.5", {"start": v(3.42, -11.47) * mm, "mid": v(3.1, -11.08) * mm, "end": v(2.84, -10.67) * mm});
            skArc(sketch, "E40.25.6", {"start": v(2.84, -10.67) * mm, "mid": v(2.81, -10.65) * mm, "end": v(2.78, -10.64) * mm});
            skArc(sketch, "E40.26.0", {"start": v(5.23, -9.68) * mm, "mid": v(5.21, -9.7) * mm, "end": v(5.2, -9.73) * mm});
            skArc(sketch, "E40.26.1", {"start": v(5.33, -10.72) * mm, "mid": v(5.3, -10.22) * mm, "end": v(5.2, -9.73) * mm});
            skArc(sketch, "E40.26.2", {"start": v(5.3, -10.76) * mm, "mid": v(5.33, -10.74) * mm, "end": v(5.33, -10.72) * mm});
            skArc(sketch, "E40.26.3", {"start": v(5.3, -10.76) * mm, "mid": v(5.15, -10.84) * mm, "end": v(5, -10.9) * mm});
            skArc(sketch, "E40.26.4", {"start": v(4.95, -10.9) * mm, "mid": v(4.97, -10.91) * mm, "end": v(5, -10.9) * mm});
            skArc(sketch, "E40.26.5", {"start": v(4.95, -10.9) * mm, "mid": v(4.59, -10.56) * mm, "end": v(4.26, -10.18) * mm});
            skArc(sketch, "E40.26.6", {"start": v(4.26, -10.18) * mm, "mid": v(4.23, -10.16) * mm, "end": v(4.2, -10.17) * mm});
            skArc(sketch, "E40.27.0", {"start": v(6.5, -8.87) * mm, "mid": v(6.48, -8.9) * mm, "end": v(6.48, -8.93) * mm});
            skArc(sketch, "E40.27.1", {"start": v(6.74, -9.9) * mm, "mid": v(6.63, -9.4) * mm, "end": v(6.48, -8.93) * mm});
            skArc(sketch, "E40.27.2", {"start": v(6.72, -9.94) * mm, "mid": v(6.74, -9.92) * mm, "end": v(6.74, -9.9) * mm});
            skArc(sketch, "E40.27.3", {"start": v(6.72, -9.94) * mm, "mid": v(6.58, -10.03) * mm, "end": v(6.44, -10.13) * mm});
            skArc(sketch, "E40.27.4", {"start": v(6.38, -10.13) * mm, "mid": v(6.41, -10.13) * mm, "end": v(6.44, -10.13) * mm});
            skArc(sketch, "E40.27.5", {"start": v(6.38, -10.13) * mm, "mid": v(5.98, -9.83) * mm, "end": v(5.6, -9.5) * mm});
            skArc(sketch, "E40.27.6", {"start": v(5.6, -9.5) * mm, "mid": v(5.58, -9.5) * mm, "end": v(5.55, -9.5) * mm});
            skArc(sketch, "E40.28.0", {"start": v(7.65, -7.9) * mm, "mid": v(7.63, -7.93) * mm, "end": v(7.64, -7.96) * mm});
            skArc(sketch, "E40.28.1", {"start": v(8.03, -8.88) * mm, "mid": v(7.85, -8.41) * mm, "end": v(7.64, -7.96) * mm});
            skArc(sketch, "E40.28.2", {"start": v(8.01, -8.93) * mm, "mid": v(8.03, -8.9) * mm, "end": v(8.03, -8.88) * mm});
            skArc(sketch, "E40.28.3", {"start": v(8.01, -8.93) * mm, "mid": v(7.89, -9.04) * mm, "end": v(7.76, -9.15) * mm});
            skArc(sketch, "E40.28.4", {"start": v(7.7, -9.16) * mm, "mid": v(7.73, -9.17) * mm, "end": v(7.76, -9.15) * mm});
            skArc(sketch, "E40.28.5", {"start": v(7.7, -9.16) * mm, "mid": v(7.27, -8.93) * mm, "end": v(6.85, -8.65) * mm});
            skArc(sketch, "E40.28.6", {"start": v(6.85, -8.65) * mm, "mid": v(6.82, -8.64) * mm, "end": v(6.79, -8.65) * mm});
            skArc(sketch, "E40.29.0", {"start": v(8.65, -6.79) * mm, "mid": v(8.64, -6.82) * mm, "end": v(8.65, -6.85) * mm});
            skArc(sketch, "E40.29.1", {"start": v(9.16, -7.7) * mm, "mid": v(8.93, -7.27) * mm, "end": v(8.65, -6.85) * mm});
            skArc(sketch, "E40.29.2", {"start": v(9.15, -7.76) * mm, "mid": v(9.17, -7.73) * mm, "end": v(9.16, -7.7) * mm});
            skArc(sketch, "E40.29.3", {"start": v(9.15, -7.76) * mm, "mid": v(9.04, -7.89) * mm, "end": v(8.93, -8.01) * mm});
            skArc(sketch, "E40.29.4", {"start": v(8.88, -8.03) * mm, "mid": v(8.9, -8.03) * mm, "end": v(8.93, -8.01) * mm});
            skArc(sketch, "E40.29.5", {"start": v(8.88, -8.03) * mm, "mid": v(8.41, -7.85) * mm, "end": v(7.96, -7.64) * mm});
            skArc(sketch, "E40.29.6", {"start": v(7.96, -7.64) * mm, "mid": v(7.93, -7.63) * mm, "end": v(7.9, -7.65) * mm});
            skArc(sketch, "E40.30.0", {"start": v(9.5, -5.55) * mm, "mid": v(9.5, -5.58) * mm, "end": v(9.5, -5.6) * mm});
            skArc(sketch, "E40.30.1", {"start": v(10.13, -6.38) * mm, "mid": v(9.83, -5.98) * mm, "end": v(9.5, -5.6) * mm});
            skArc(sketch, "E40.30.2", {"start": v(10.13, -6.44) * mm, "mid": v(10.13, -6.41) * mm, "end": v(10.13, -6.38) * mm});
            skArc(sketch, "E40.30.3", {"start": v(10.13, -6.44) * mm, "mid": v(10.03, -6.58) * mm, "end": v(9.94, -6.72) * mm});
            skArc(sketch, "E40.30.4", {"start": v(9.9, -6.74) * mm, "mid": v(9.92, -6.74) * mm, "end": v(9.94, -6.72) * mm});
            skArc(sketch, "E40.30.5", {"start": v(9.9, -6.74) * mm, "mid": v(9.4, -6.63) * mm, "end": v(8.93, -6.48) * mm});
            skArc(sketch, "E40.30.6", {"start": v(8.93, -6.48) * mm, "mid": v(8.9, -6.48) * mm, "end": v(8.87, -6.5) * mm});
            skArc(sketch, "E40.31.0", {"start": v(10.17, -4.2) * mm, "mid": v(10.16, -4.23) * mm, "end": v(10.18, -4.26) * mm});
            skArc(sketch, "E40.31.1", {"start": v(10.9, -4.95) * mm, "mid": v(10.56, -4.59) * mm, "end": v(10.18, -4.26) * mm});
            skArc(sketch, "E40.31.2", {"start": v(10.9, -5) * mm, "mid": v(10.91, -4.97) * mm, "end": v(10.9, -4.95) * mm});
            skArc(sketch, "E40.31.3", {"start": v(10.9, -5) * mm, "mid": v(10.84, -5.15) * mm, "end": v(10.76, -5.3) * mm});
            skArc(sketch, "E40.31.4", {"start": v(10.72, -5.33) * mm, "mid": v(10.74, -5.33) * mm, "end": v(10.76, -5.3) * mm});
            skArc(sketch, "E40.31.5", {"start": v(10.72, -5.33) * mm, "mid": v(10.22, -5.3) * mm, "end": v(9.73, -5.2) * mm});
            skArc(sketch, "E40.31.6", {"start": v(9.73, -5.2) * mm, "mid": v(9.7, -5.21) * mm, "end": v(9.68, -5.23) * mm});
            skArc(sketch, "E40.32.0", {"start": v(10.64, -2.78) * mm, "mid": v(10.65, -2.81) * mm, "end": v(10.67, -2.84) * mm});
            skArc(sketch, "E40.32.1", {"start": v(11.47, -3.42) * mm, "mid": v(11.08, -3.1) * mm, "end": v(10.67, -2.84) * mm});
            skArc(sketch, "E40.32.2", {"start": v(11.49, -3.47) * mm, "mid": v(11.49, -3.44) * mm, "end": v(11.47, -3.42) * mm});
            skArc(sketch, "E40.32.3", {"start": v(11.49, -3.47) * mm, "mid": v(11.44, -3.63) * mm, "end": v(11.39, -3.8) * mm});
            skArc(sketch, "E40.32.4", {"start": v(11.34, -3.82) * mm, "mid": v(11.37, -3.81) * mm, "end": v(11.39, -3.8) * mm});
            skArc(sketch, "E40.32.5", {"start": v(11.34, -3.82) * mm, "mid": v(10.85, -3.85) * mm, "end": v(10.35, -3.83) * mm});
            skArc(sketch, "E40.32.6", {"start": v(10.35, -3.83) * mm, "mid": v(10.32, -3.84) * mm, "end": v(10.3, -3.87) * mm});
            skArc(sketch, "E40.33.0", {"start": v(10.92, -1.3) * mm, "mid": v(10.93, -1.34) * mm, "end": v(10.95, -1.36) * mm});
            skArc(sketch, "E40.33.1", {"start": v(11.83, -1.82) * mm, "mid": v(11.4, -1.57) * mm, "end": v(10.95, -1.36) * mm});
            skArc(sketch, "E40.33.2", {"start": v(11.85, -1.87) * mm, "mid": v(11.85, -1.84) * mm, "end": v(11.83, -1.82) * mm});
            skArc(sketch, "E40.33.3", {"start": v(11.85, -1.87) * mm, "mid": v(11.83, -2.04) * mm, "end": v(11.8, -2.2) * mm});
            skArc(sketch, "E40.33.4", {"start": v(11.76, -2.24) * mm, "mid": v(11.78, -2.23) * mm, "end": v(11.8, -2.2) * mm});
            skArc(sketch, "E40.33.5", {"start": v(11.76, -2.24) * mm, "mid": v(11.27, -2.34) * mm, "end": v(10.77, -2.39) * mm});
            skArc(sketch, "E40.33.6", {"start": v(10.77, -2.39) * mm, "mid": v(10.75, -2.4) * mm, "end": v(10.73, -2.43) * mm});
            skArc(sketch, "E40.34.0", {"start": v(11, 0.2) * mm, "mid": v(11, 0.16) * mm, "end": v(11.04, 0.15) * mm});
            skArc(sketch, "E40.34.1", {"start": v(11.97, -0.2) * mm, "mid": v(11.5, 0) * mm, "end": v(11.04, 0.15) * mm});
            skArc(sketch, "E40.34.2", {"start": v(12, -0.24) * mm, "mid": v(12, -0.21) * mm, "end": v(11.97, -0.2) * mm});
            skArc(sketch, "E40.34.3", {"start": v(12, -0.24) * mm, "mid": v(12, -0.4) * mm, "end": v(11.99, -0.58) * mm});
            skArc(sketch, "E40.34.4", {"start": v(11.95, -0.62) * mm, "mid": v(11.98, -0.6) * mm, "end": v(11.99, -0.58) * mm});
            skArc(sketch, "E40.34.5", {"start": v(11.95, -0.62) * mm, "mid": v(11.48, -0.78) * mm, "end": v(11, -0.9) * mm});
            skArc(sketch, "E40.34.6", {"start": v(11, -0.9) * mm, "mid": v(10.97, -0.92) * mm, "end": v(10.96, -0.94) * mm});
            skArc(sketch, "E40.35.0", {"start": v(10.87, 1.7) * mm, "mid": v(10.88, 1.66) * mm, "end": v(10.91, 1.65) * mm});
            skArc(sketch, "E40.35.1", {"start": v(11.88, 1.44) * mm, "mid": v(11.4, 1.56) * mm, "end": v(10.91, 1.65) * mm});
            skArc(sketch, "E40.35.2", {"start": v(11.92, 1.4) * mm, "mid": v(11.9, 1.42) * mm, "end": v(11.88, 1.44) * mm});
            skArc(sketch, "E40.35.3", {"start": v(11.92, 1.4) * mm, "mid": v(11.94, 1.23) * mm, "end": v(11.95, 1.06) * mm});
            skArc(sketch, "E40.35.4", {"start": v(11.93, 1.01) * mm, "mid": v(11.95, 1.03) * mm, "end": v(11.95, 1.06) * mm});
            skArc(sketch, "E40.35.5", {"start": v(11.93, 1.01) * mm, "mid": v(11.48, 0.79) * mm, "end": v(11.02, 0.6) * mm});
            skArc(sketch, "E40.35.6", {"start": v(11.02, 0.6) * mm, "mid": v(11, 0.59) * mm, "end": v(10.99, 0.56) * mm});
            skArc(sketch, "E40.36.0", {"start": v(10.54, 3.15) * mm, "mid": v(10.56, 3.13) * mm, "end": v(10.59, 3.12) * mm});
            skArc(sketch, "E40.36.1", {"start": v(11.58, 3.04) * mm, "mid": v(11.08, 3.1) * mm, "end": v(10.59, 3.12) * mm});
            skArc(sketch, "E40.36.2", {"start": v(11.62, 3) * mm, "mid": v(11.6, 3.03) * mm, "end": v(11.58, 3.04) * mm});
            skArc(sketch, "E40.36.3", {"start": v(11.62, 3) * mm, "mid": v(11.66, 2.84) * mm, "end": v(11.7, 2.68) * mm});
            skArc(sketch, "E40.36.4", {"start": v(11.68, 2.63) * mm, "mid": v(11.7, 2.65) * mm, "end": v(11.7, 2.68) * mm});
            skArc(sketch, "E40.36.5", {"start": v(11.68, 2.63) * mm, "mid": v(11.27, 2.35) * mm, "end": v(10.83, 2.1) * mm});
            skArc(sketch, "E40.36.6", {"start": v(10.83, 2.1) * mm, "mid": v(10.81, 2.08) * mm, "end": v(10.8, 2.05) * mm});
            skArc(sketch, "E40.37.0", {"start": v(10.01, 4.56) * mm, "mid": v(10.03, 4.54) * mm, "end": v(10.06, 4.53) * mm});
            skArc(sketch, "E40.37.1", {"start": v(11.06, 4.6) * mm, "mid": v(10.56, 4.58) * mm, "end": v(10.06, 4.53) * mm});
            skArc(sketch, "E40.37.2", {"start": v(11.1, 4.56) * mm, "mid": v(11.08, 4.58) * mm, "end": v(11.06, 4.6) * mm});
            skArc(sketch, "E40.37.3", {"start": v(11.1, 4.56) * mm, "mid": v(11.16, 4.4) * mm, "end": v(11.22, 4.24) * mm});
            skArc(sketch, "E40.37.4", {"start": v(11.21, 4.2) * mm, "mid": v(11.23, 4.22) * mm, "end": v(11.22, 4.24) * mm});
            skArc(sketch, "E40.37.5", {"start": v(11.21, 4.2) * mm, "mid": v(10.84, 3.86) * mm, "end": v(10.45, 3.56) * mm});
            skArc(sketch, "E40.37.6", {"start": v(10.45, 3.56) * mm, "mid": v(10.43, 3.53) * mm, "end": v(10.43, 3.5) * mm});
            skArc(sketch, "E40.38.0", {"start": v(9.3, 5.88) * mm, "mid": v(9.32, 5.86) * mm, "end": v(9.35, 5.86) * mm});
            skArc(sketch, "E40.38.1", {"start": v(10.33, 6.05) * mm, "mid": v(9.84, 5.98) * mm, "end": v(9.35, 5.86) * mm});
            skArc(sketch, "E40.38.2", {"start": v(10.38, 6.03) * mm, "mid": v(10.36, 6.05) * mm, "end": v(10.33, 6.05) * mm});
            skArc(sketch, "E40.38.3", {"start": v(10.38, 6.03) * mm, "mid": v(10.46, 5.88) * mm, "end": v(10.54, 5.73) * mm});
            skArc(sketch, "E40.38.4", {"start": v(10.54, 5.68) * mm, "mid": v(10.55, 5.7) * mm, "end": v(10.54, 5.73) * mm});
            skArc(sketch, "E40.38.5", {"start": v(10.54, 5.68) * mm, "mid": v(10.22, 5.3) * mm, "end": v(9.87, 4.95) * mm});
            skArc(sketch, "E40.38.6", {"start": v(9.87, 4.95) * mm, "mid": v(9.85, 4.92) * mm, "end": v(9.85, 4.89) * mm});
            skArc(sketch, "E40.39.0", {"start": v(8.4, 7.1) * mm, "mid": v(8.44, 7.08) * mm, "end": v(8.47, 7.08) * mm});
            skArc(sketch, "E40.39.1", {"start": v(9.4, 7.4) * mm, "mid": v(8.93, 7.26) * mm, "end": v(8.47, 7.08) * mm});
            skArc(sketch, "E40.39.2", {"start": v(9.46, 7.38) * mm, "mid": v(9.44, 7.4) * mm, "end": v(9.4, 7.4) * mm});
            skArc(sketch, "E40.39.3", {"start": v(9.46, 7.38) * mm, "mid": v(9.56, 7.25) * mm, "end": v(9.66, 7.12) * mm});
            skArc(sketch, "E40.39.4", {"start": v(9.67, 7.06) * mm, "mid": v(9.67, 7.09) * mm, "end": v(9.66, 7.12) * mm});
            skArc(sketch, "E40.39.5", {"start": v(9.67, 7.06) * mm, "mid": v(9.4, 6.64) * mm, "end": v(9.1, 6.24) * mm});
            skArc(sketch, "E40.39.6", {"start": v(9.1, 6.24) * mm, "mid": v(9.09, 6.21) * mm, "end": v(9.1, 6.18) * mm});
            skArc(sketch, "E40.40.0", {"start": v(7.36, 8.17) * mm, "mid": v(7.4, 8.16) * mm, "end": v(7.42, 8.17) * mm});
            skArc(sketch, "E40.40.1", {"start": v(8.31, 8.61) * mm, "mid": v(7.86, 8.4) * mm, "end": v(7.42, 8.17) * mm});
            skArc(sketch, "E40.40.2", {"start": v(8.36, 8.6) * mm, "mid": v(8.34, 8.62) * mm, "end": v(8.31, 8.61) * mm});
            skArc(sketch, "E40.40.3", {"start": v(8.36, 8.6) * mm, "mid": v(8.49, 8.49) * mm, "end": v(8.6, 8.36) * mm});
            skArc(sketch, "E40.40.4", {"start": v(8.61, 8.31) * mm, "mid": v(8.62, 8.34) * mm, "end": v(8.6, 8.36) * mm});
            skArc(sketch, "E40.40.5", {"start": v(8.61, 8.31) * mm, "mid": v(8.4, 7.86) * mm, "end": v(8.17, 7.42) * mm});
            skArc(sketch, "E40.40.6", {"start": v(8.17, 7.42) * mm, "mid": v(8.16, 7.4) * mm, "end": v(8.17, 7.36) * mm});
            skArc(sketch, "E40.41.0", {"start": v(6.18, 9.1) * mm, "mid": v(6.21, 9.09) * mm, "end": v(6.24, 9.1) * mm});
            skArc(sketch, "E40.41.1", {"start": v(7.06, 9.67) * mm, "mid": v(6.64, 9.4) * mm, "end": v(6.24, 9.1) * mm});
            skArc(sketch, "E40.41.2", {"start": v(7.12, 9.66) * mm, "mid": v(7.09, 9.67) * mm, "end": v(7.06, 9.67) * mm});
            skArc(sketch, "E40.41.3", {"start": v(7.12, 9.66) * mm, "mid": v(7.25, 9.56) * mm, "end": v(7.38, 9.46) * mm});
            skArc(sketch, "E40.41.4", {"start": v(7.4, 9.4) * mm, "mid": v(7.4, 9.44) * mm, "end": v(7.38, 9.46) * mm});
            skArc(sketch, "E40.41.5", {"start": v(7.4, 9.4) * mm, "mid": v(7.26, 8.93) * mm, "end": v(7.08, 8.47) * mm});
            skArc(sketch, "E40.41.6", {"start": v(7.08, 8.47) * mm, "mid": v(7.08, 8.44) * mm, "end": v(7.1, 8.4) * mm});
            skArc(sketch, "E40.42.0", {"start": v(4.89, 9.85) * mm, "mid": v(4.92, 9.85) * mm, "end": v(4.95, 9.87) * mm});
            skArc(sketch, "E40.42.1", {"start": v(5.68, 10.54) * mm, "mid": v(5.3, 10.22) * mm, "end": v(4.95, 9.87) * mm});
            skArc(sketch, "E40.42.2", {"start": v(5.73, 10.54) * mm, "mid": v(5.7, 10.55) * mm, "end": v(5.68, 10.54) * mm});
            skArc(sketch, "E40.42.3", {"start": v(5.73, 10.54) * mm, "mid": v(5.88, 10.46) * mm, "end": v(6.03, 10.38) * mm});
            skArc(sketch, "E40.42.4", {"start": v(6.05, 10.33) * mm, "mid": v(6.05, 10.36) * mm, "end": v(6.03, 10.38) * mm});
            skArc(sketch, "E40.42.5", {"start": v(6.05, 10.33) * mm, "mid": v(5.98, 9.84) * mm, "end": v(5.86, 9.35) * mm});
            skArc(sketch, "E40.42.6", {"start": v(5.86, 9.35) * mm, "mid": v(5.86, 9.32) * mm, "end": v(5.88, 9.3) * mm});
            skArc(sketch, "E40.43.0", {"start": v(3.5, 10.43) * mm, "mid": v(3.53, 10.43) * mm, "end": v(3.56, 10.45) * mm});
            skArc(sketch, "E40.43.1", {"start": v(4.2, 11.21) * mm, "mid": v(3.86, 10.84) * mm, "end": v(3.56, 10.45) * mm});
            skArc(sketch, "E40.43.2", {"start": v(4.24, 11.22) * mm, "mid": v(4.22, 11.23) * mm, "end": v(4.2, 11.21) * mm});
            skArc(sketch, "E40.43.3", {"start": v(4.24, 11.22) * mm, "mid": v(4.4, 11.16) * mm, "end": v(4.56, 11.1) * mm});
            skArc(sketch, "E40.43.4", {"start": v(4.6, 11.06) * mm, "mid": v(4.58, 11.08) * mm, "end": v(4.56, 11.1) * mm});
            skArc(sketch, "E40.43.5", {"start": v(4.6, 11.06) * mm, "mid": v(4.58, 10.56) * mm, "end": v(4.53, 10.06) * mm});
            skArc(sketch, "E40.43.6", {"start": v(4.53, 10.06) * mm, "mid": v(4.54, 10.03) * mm, "end": v(4.56, 10.01) * mm});
            skArc(sketch, "E40.44.0", {"start": v(2.05, 10.8) * mm, "mid": v(2.08, 10.81) * mm, "end": v(2.1, 10.83) * mm});
            skArc(sketch, "E40.44.1", {"start": v(2.63, 11.68) * mm, "mid": v(2.35, 11.27) * mm, "end": v(2.1, 10.83) * mm});
            skArc(sketch, "E40.44.2", {"start": v(2.68, 11.7) * mm, "mid": v(2.65, 11.7) * mm, "end": v(2.63, 11.68) * mm});
            skArc(sketch, "E40.44.3", {"start": v(2.68, 11.7) * mm, "mid": v(2.84, 11.66) * mm, "end": v(3, 11.62) * mm});
            skArc(sketch, "E40.44.4", {"start": v(3.04, 11.58) * mm, "mid": v(3.03, 11.6) * mm, "end": v(3, 11.62) * mm});
            skArc(sketch, "E40.44.5", {"start": v(3.04, 11.58) * mm, "mid": v(3.1, 11.08) * mm, "end": v(3.12, 10.59) * mm});
            skArc(sketch, "E40.44.6", {"start": v(3.12, 10.59) * mm, "mid": v(3.13, 10.56) * mm, "end": v(3.15, 10.54) * mm});
            skArc(sketch, "E40.45.0", {"start": v(0.56, 10.99) * mm, "mid": v(0.59, 11) * mm, "end": v(0.6, 11.02) * mm});
            skArc(sketch, "E40.45.1", {"start": v(1.01, 11.93) * mm, "mid": v(0.79, 11.48) * mm, "end": v(0.6, 11.02) * mm});
            skArc(sketch, "E40.45.2", {"start": v(1.06, 11.95) * mm, "mid": v(1.03, 11.95) * mm, "end": v(1.01, 11.93) * mm});
            skArc(sketch, "E40.45.3", {"start": v(1.06, 11.95) * mm, "mid": v(1.23, 11.94) * mm, "end": v(1.4, 11.92) * mm});
            skArc(sketch, "E40.45.4", {"start": v(1.44, 11.88) * mm, "mid": v(1.42, 11.9) * mm, "end": v(1.4, 11.92) * mm});
            skArc(sketch, "E40.45.5", {"start": v(1.44, 11.88) * mm, "mid": v(1.56, 11.4) * mm, "end": v(1.65, 10.91) * mm});
            skArc(sketch, "E40.45.6", {"start": v(1.65, 10.91) * mm, "mid": v(1.66, 10.88) * mm, "end": v(1.7, 10.87) * mm});
            skSolve(sketch);
        }
        {
            var Q0;
            Q0=makeQuery(id+"F6.imprint","IMPRINT",FACE,{"disambiguationData":[TD([[makeQuery(id+"F6.imprint","IMPRINT",EDGE,{"derivedFrom":sQuery(id+"F6.wireOp",EDGE,"E20")}),1.0]])]});
            extrude(context, id + "F7", {"entities" : qUnion([Q0]), "operationType" : NewBodyOperationType.REMOVE, "oppositeDirection" : true, "depth" : 1.5 * mm});
        }
    });
